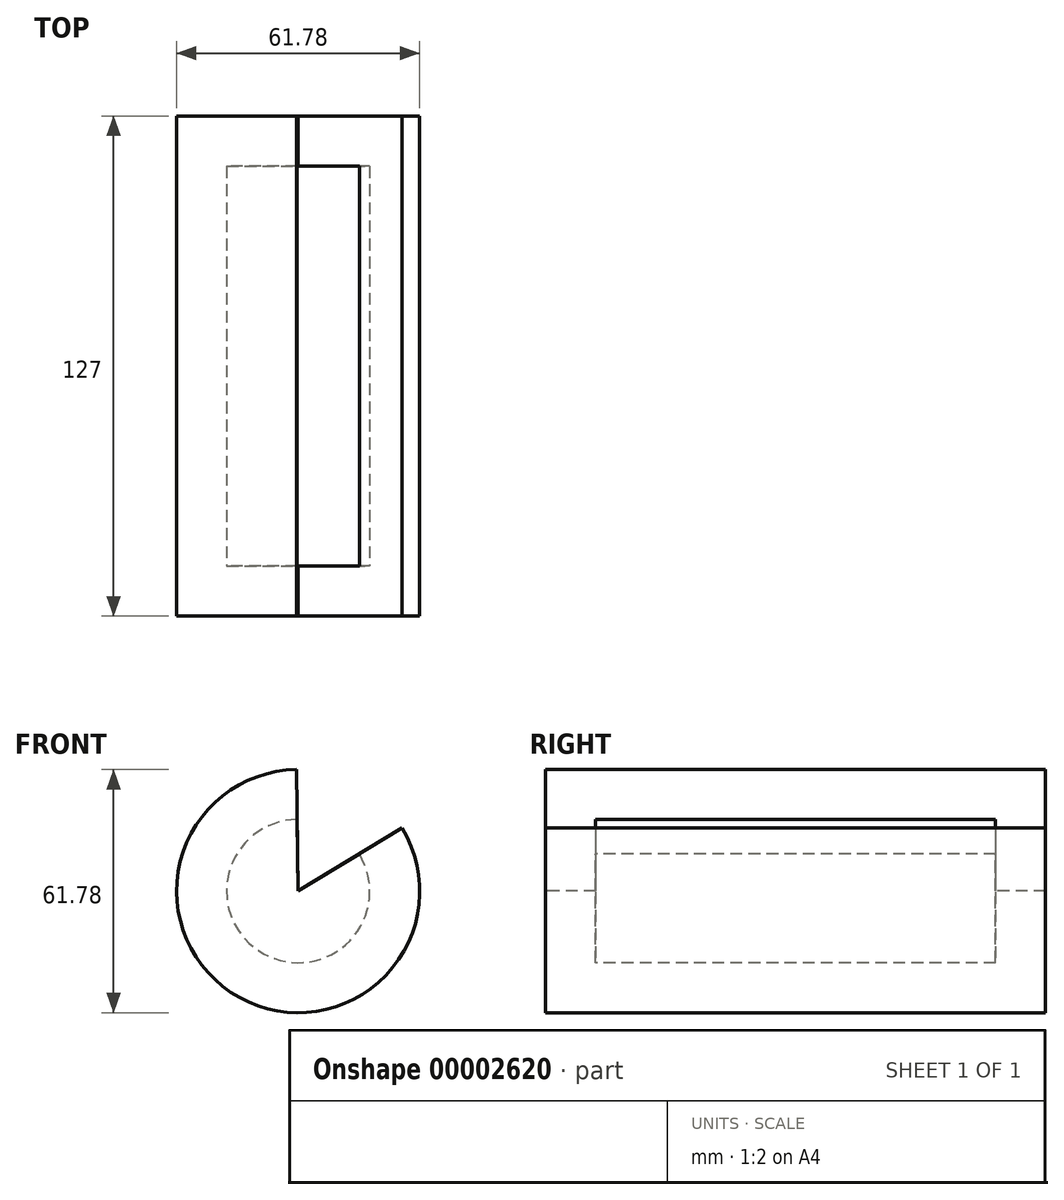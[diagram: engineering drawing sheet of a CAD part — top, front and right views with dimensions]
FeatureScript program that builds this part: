
annotation { "Feature Type Name" : "Feature", "Feature Type Description" : "" }
export const myFeature = defineFeature(function(context is Context, id is Id, definition is map)
    precondition{}
    {
        {
            var Q0;
            Q0=qCreatedBy(makeId("Front.planeOp"),FACE);
            var sketch = newSketch(context, id + "F0", { "sketchPlane" : qUnion([Q0])});
            skArc(sketch, "E0", {"start": v(-0.46, 30.89) * mm, "mid": v(-14.95, -27.03) * mm, "end": v(26.4, 16.03) * mm});
            skLineSegment(sketch, "E1", {"start": v(-0.46, 30.89) * mm, "end": v(0, 0) * mm});
            skLineSegment(sketch, "E2", {"start": v(0, 0) * mm, "end": v(26.4, 16.03) * mm});
            skSolve(sketch);
        }
        {
            var Q0;
            Q0=makeQuery(id+"F0.imprint","IMPRINT",FACE,{"disambiguationData":[TD([[makeQuery(id+"F0.imprint","IMPRINT",EDGE,{"derivedFrom":sQuery(id+"F0.wireOp",EDGE,"59b115f4-471a-4e64-8025-10e50ad705b2")}),1.0]])]});
            var Q1;
            Q1=makeQuery(id+"F0.imprint","IMPRINT",FACE,{"disambiguationData":[TD([[makeQuery(id+"F0.imprint","IMPRINT",EDGE,{"derivedFrom":sQuery(id+"F0.wireOp",EDGE,"E0")}),1.0]])]});
            extrude(context, id + "F1", {"entities" : qUnion([Q0, Q1]), "oppositeDirection" : true, "depth" : 127 * mm});
        }
        {
            var Q0;
            Q0=makeQuery(id+"F1.opExtrude","SWEPT_FACE",FACE,{"disambiguationData":[OSD([sQuery(id+"F0.wireOp",EDGE,"E1")])]});
            var Q1;
            Q1=makeQuery(id+"F1.opExtrude","SWEPT_FACE",FACE,{"disambiguationData":[OSD([sQuery(id+"F0.wireOp",EDGE,"E2")])]});
            shell(context, id + "F2", {"entities" : qUnion([Q0, Q1]), "thickness" : 12.7 * mm});
        }
    });
